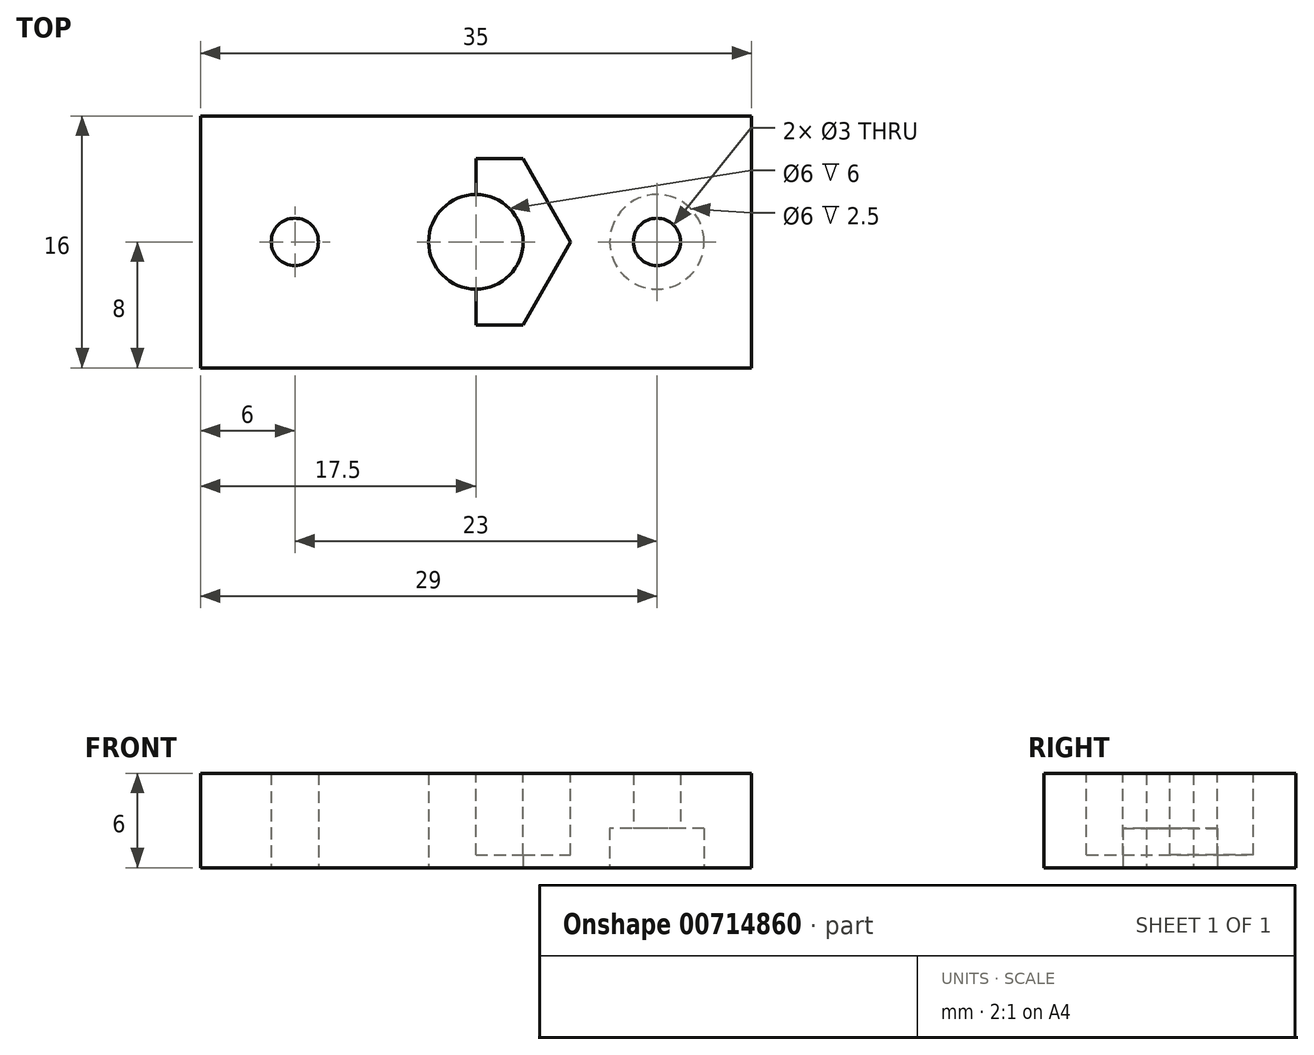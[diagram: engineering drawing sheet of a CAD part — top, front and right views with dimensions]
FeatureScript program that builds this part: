
annotation { "Feature Type Name" : "Feature", "Feature Type Description" : "" }
export const myFeature = defineFeature(function(context is Context, id is Id, definition is map)
    precondition{}
    {
        {
            var Q0;
            Q0=qCreatedBy(makeId("Top.planeOp"),FACE);
            var sketch = newSketch(context, id + "F0", { "sketchPlane" : qUnion([Q0])});
            skLineSegment(sketch, "E0.bottom", {"start": v(0, 0) * mm, "end": v(-35, 0) * mm});
            skLineSegment(sketch, "E0.top", {"start": v(0, 16) * mm, "end": v(-35, 16) * mm});
            skLineSegment(sketch, "E0.left", {"start": v(0, 0) * mm, "end": v(0, 16) * mm});
            skLineSegment(sketch, "E0.right", {"start": v(-35, 0) * mm, "end": v(-35, 16) * mm});
            skPoint(sketch, "E1.endSnap0", {"position": v(-35, 8) * mm});
            skCircle(sketch, "E2", {"center": v(-17.5, 8) * mm, "radius": 3 * mm});
            skPoint(sketch, "E3.endSnap0", {"position": v(0, 8) * mm});
            skCircle(sketch, "E4", {"center": v(-6, 8) * mm, "radius": 1.5 * mm});
            skCircle(sketch, "E5.MirrorC", {"center": v(-29, 8) * mm, "radius": 1.5 * mm});
            skSolve(sketch);
        }
        {
            var Q0;
            Q0=makeQuery(id+"F0.imprint","IMPRINT",FACE,{"disambiguationData":[TD([[makeQuery(id+"F0.imprint","IMPRINT",EDGE,{"derivedFrom":sQuery(id+"F0.wireOp",EDGE,"E0.bottom")}),-1.0]])]});
            extrude(context, id + "F1", {"entities" : qUnion([Q0]), "depth" : 6 * mm, "offsetDistance" : 25 * mm});
        }
        {
            var Q0;
            Q0=makeQuery(id+"F1.opExtrude","CAP_FACE",FACE,{"disambiguationData":[OSD([sQuery(id+"F0.wireOp",EDGE,"E0.bottom"),sQuery(id+"F0.wireOp",EDGE,"E0.top"),sQuery(id+"F0.wireOp",EDGE,"E0.left"),sQuery(id+"F0.wireOp",EDGE,"E0.right"),sQuery(id+"F0.wireOp",EDGE,"E2"),sQuery(id+"F0.wireOp",EDGE,"E4"),sQuery(id+"F0.wireOp",EDGE,"E5.MirrorC")])],"isStart":false});
            var sketch = newSketch(context, id + "F2", { "sketchPlane" : qUnion([Q0])});
            skCircle(sketch, "E6", {"center": v(-6, 8) * mm, "radius": 3 * mm});
            skLineSegment(sketch, "E7", {"start": v(-17.5, 0) * mm, "end": v(-17.5, 16) * mm});
            skCircle(sketch, "E8.MirrorC", {"center": v(-29, 8) * mm, "radius": 3 * mm});
            skLineSegment(sketch, "E9", {"start": v(-17.5, 8) * mm, "end": v(-14.5, 8) * mm});
            skLineSegment(sketch, "E10", {"start": v(-14.5, 8) * mm, "end": v(-11.5, 8) * mm});
            skLineSegment(sketch, "E11", {"start": v(-17.5, 5) * mm, "end": v(-17.5, 2.7) * mm});
            skLineSegment(sketch, "E12", {"start": v(-17.5, 2.7) * mm, "end": v(-14.5, 2.7) * mm});
            skLineSegment(sketch, "E13", {"start": v(-14.5, 2.7) * mm, "end": v(-11.5, 8) * mm});
            skLineSegment(sketch, "E14.MirrorCS", {"start": v(-17.5, 13.3) * mm, "end": v(-14.5, 13.3) * mm});
            skLineSegment(sketch, "E15.MirrorCS", {"start": v(-14.5, 13.3) * mm, "end": v(-11.5, 8) * mm});
            skLineSegment(sketch, "E16.MirrorCS", {"start": v(-17.5, 13.3) * mm, "end": v(-20.5, 13.3) * mm});
            skLineSegment(sketch, "E17.MirrorCS", {"start": v(-20.5, 13.3) * mm, "end": v(-23.5, 8) * mm});
            skLineSegment(sketch, "E18.MirrorCS", {"start": v(-20.5, 2.7) * mm, "end": v(-23.5, 8) * mm});
            skLineSegment(sketch, "E19.MirrorCS", {"start": v(-17.5, 2.7) * mm, "end": v(-20.5, 2.7) * mm});
            skSolve(sketch);
        }
        {
            var Q0;
            {var subQ4=sQuery(id+"F2.wireOp",EDGE,"E11");Q0=makeQuery(id+"F2.imprint","IMPRINT",FACE,{"disambiguationData":[TD([[makeQuery(id+"F2.imprint","IMPRINT",EDGE,{"derivedFrom":subQ4}),-1.0]])]});}
            var Q1;
            {var subQ1=sQuery(id+"F2.wireOp",EDGE,"E10");Q1=makeQuery(id+"F2.imprint","IMPRINT",FACE,{"disambiguationData":[TD([[makeQuery(id+"F2.imprint","IMPRINT",EDGE,{"derivedFrom":subQ1}),1.0]])]});}
            var Q2;
            {var subQ1=sQuery(id+"F2.wireOp",EDGE,"E10");Q2=makeQuery(id+"F2.imprint","IMPRINT",FACE,{"disambiguationData":[TD([[makeQuery(id+"F2.imprint","IMPRINT",EDGE,{"derivedFrom":subQ1}),-1.0]])]});}
            extrude(context, id + "F3", {"entities" : qUnion([Q0, Q1, Q2]), "operationType" : NewBodyOperationType.REMOVE, "oppositeDirection" : true, "depth" : 5.2 * mm, "offsetDistance" : 25 * mm});
        }
        {
            var Q0;
            Q0=qCreatedBy(makeId("Top.planeOp"),FACE);
            var sketch = newSketch(context, id + "F4", { "sketchPlane" : qUnion([Q0])});
            skCircle(sketch, "E20", {"center": v(-6, 8) * mm, "radius": 3 * mm});
            skLineSegment(sketch, "E21", {"start": v(-17.5, 0) * mm, "end": v(-17.5, 8) * mm});
            skCircle(sketch, "E22.MirrorC", {"center": v(-29, 8) * mm, "radius": 3 * mm});
            skSolve(sketch);
        }
        {
            var Q0;
            Q0=makeQuery(id+"F4.imprint","IMPRINT",FACE,{"disambiguationData":[TD([[makeQuery(id+"F4.imprint","IMPRINT",EDGE,{"derivedFrom":sQuery(id+"F4.wireOp",EDGE,"E22.MirrorC")}),-1.0]])]});
            var Q1;
            Q1=makeQuery(id+"F4.imprint","IMPRINT",FACE,{"disambiguationData":[TD([[makeQuery(id+"F4.imprint","IMPRINT",EDGE,{"derivedFrom":sQuery(id+"F4.wireOp",EDGE,"E20")}),1.0]])]});
            extrude(context, id + "F5", {"entities" : qUnion([Q0, Q1]), "operationType" : NewBodyOperationType.REMOVE, "depth" : 2.5 * mm, "offsetDistance" : 25 * mm});
        }
    });
